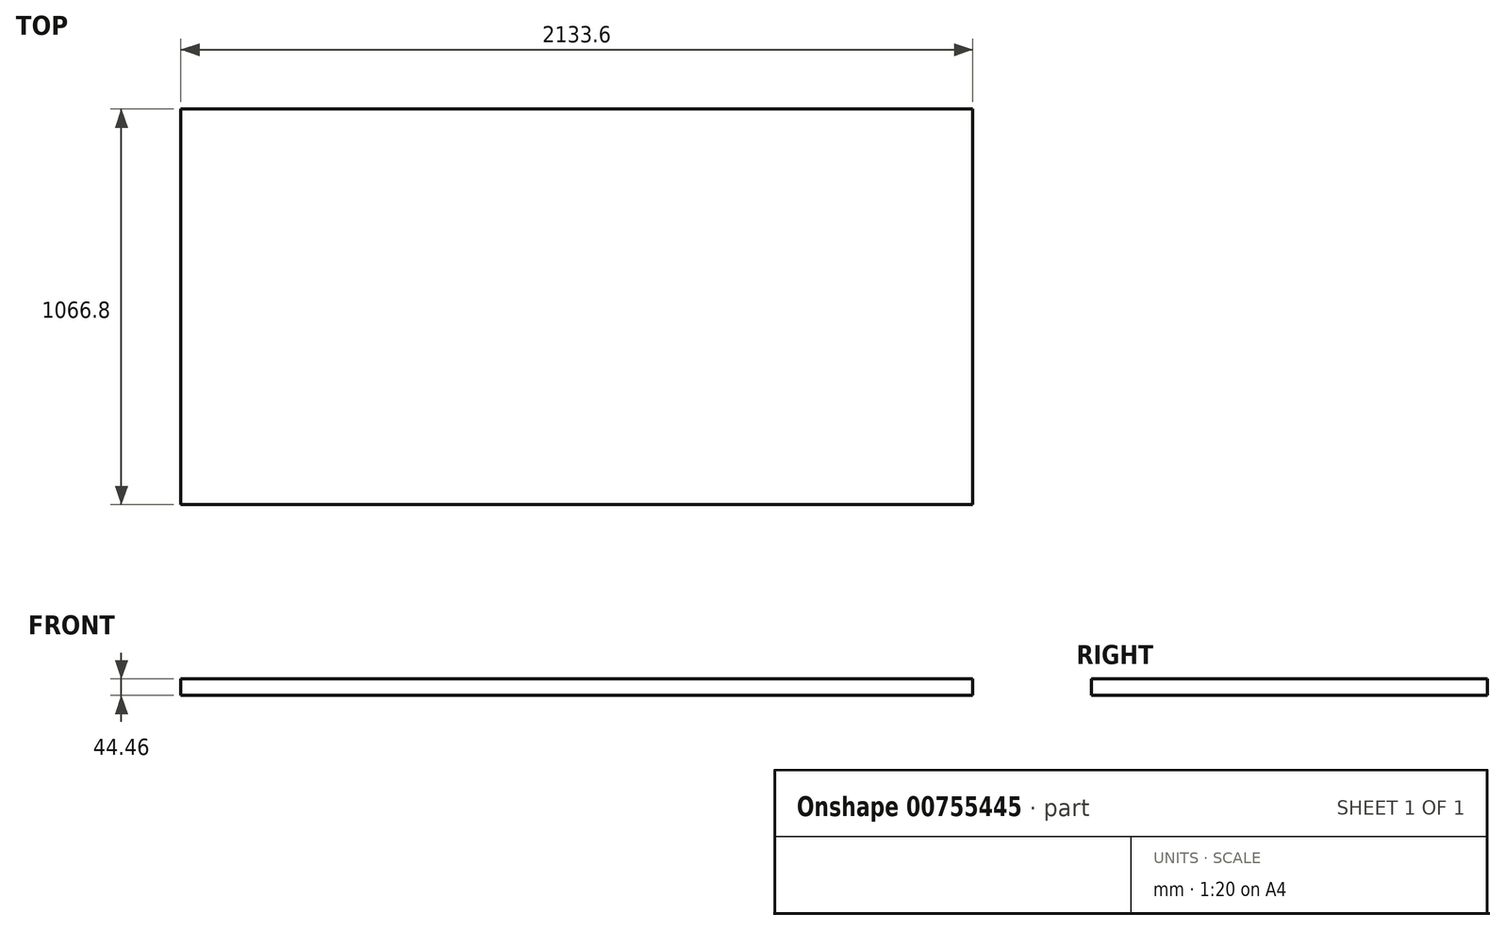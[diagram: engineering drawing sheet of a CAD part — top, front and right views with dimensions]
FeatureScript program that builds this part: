
annotation { "Feature Type Name" : "Feature", "Feature Type Description" : "" }
export const myFeature = defineFeature(function(context is Context, id is Id, definition is map)
    precondition{}
    {
        {
            var Q0;
            Q0=qCreatedBy(makeId("Top.planeOp"),FACE);
            var sketch = newSketch(context, id + "F0", { "sketchPlane" : qUnion([Q0])});
            skLineSegment(sketch, "E0.bottom", {"start": v(-1066.8, 533.4) * mm, "end": v(1066.8, 533.4) * mm});
            skLineSegment(sketch, "E0.top", {"start": v(-1066.8, -533.4) * mm, "end": v(1066.8, -533.4) * mm});
            skLineSegment(sketch, "E0.left", {"start": v(-1066.8, 533.4) * mm, "end": v(-1066.8, -533.4) * mm});
            skLineSegment(sketch, "E0.right", {"start": v(1066.8, 533.4) * mm, "end": v(1066.8, -533.4) * mm});
            skPoint(sketch, "E0.middle", {"position": v(0, 0) * mm});
            skSolve(sketch);
        }
        {
            var Q0;
            Q0 = qSketchRegion(id + "F0", true);
            extrude(context, id + "F1", {"entities" : qUnion([Q0]), "endBound" : BoundingType.SYMMETRIC, "depth" : 44.45 * mm, "offsetDistance" : 25.4 * mm});
        }
    });
